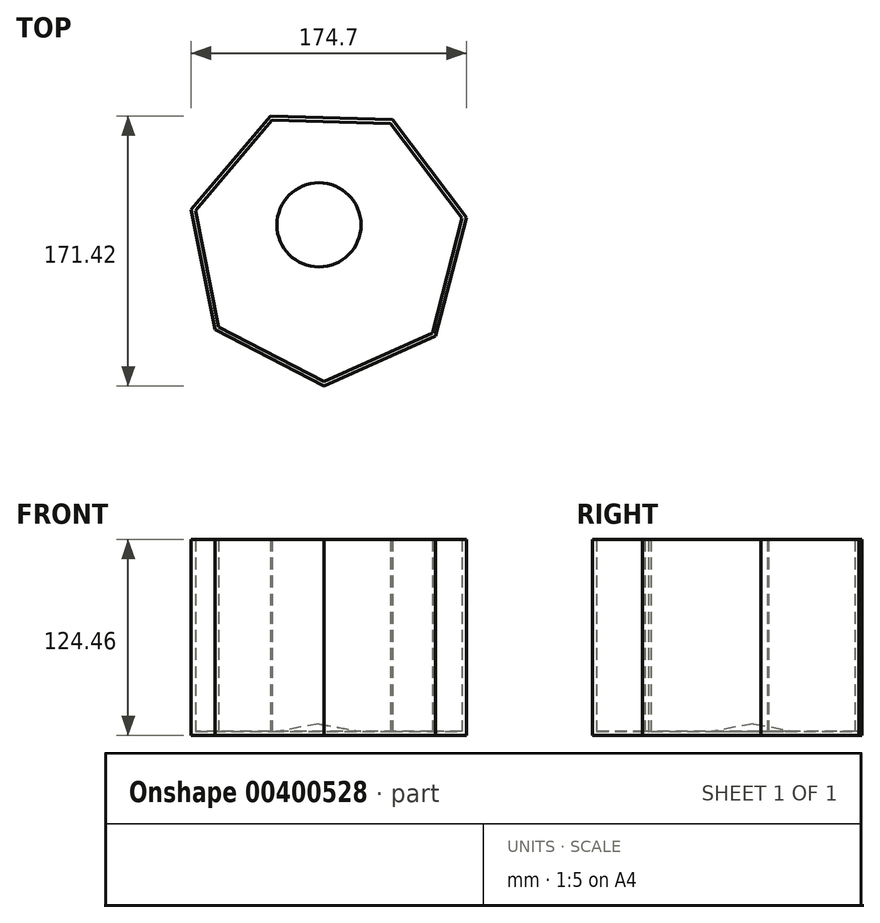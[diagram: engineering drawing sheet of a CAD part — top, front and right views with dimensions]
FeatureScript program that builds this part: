
annotation { "Feature Type Name" : "Feature", "Feature Type Description" : "" }
export const myFeature = defineFeature(function(context is Context, id is Id, definition is map)
    precondition{}
    {
        {
            var Q0;
            Q0=qCreatedBy(makeId("Top.planeOp"),FACE);
            var sketch = newSketch(context, id + "F0", { "sketchPlane" : qUnion([Q0])});
            skCircle(sketch, "E0.cCircle", {"center": v(0, 0) * mm, "radius": 80.76 * mm, "construction": true});
            skLineSegment(sketch, "E0.0", {"start": v(41.16, 79.62) * mm, "end": v(87.91, 17.47) * mm});
            skLineSegment(sketch, "E0.1", {"start": v(87.91, 17.47) * mm, "end": v(68.47, -57.84) * mm});
            skLineSegment(sketch, "E0.2", {"start": v(68.47, -57.84) * mm, "end": v(-2.54, -89.6) * mm});
            skLineSegment(sketch, "E0.3", {"start": v(-2.54, -89.6) * mm, "end": v(-71.63, -53.88) * mm});
            skLineSegment(sketch, "E0.4", {"start": v(-71.63, -53.88) * mm, "end": v(-86.79, 22.4) * mm});
            skLineSegment(sketch, "E0.5", {"start": v(-86.79, 22.4) * mm, "end": v(-36.59, 81.82) * mm});
            skLineSegment(sketch, "E0.6", {"start": v(-36.59, 81.82) * mm, "end": v(41.16, 79.62) * mm});
            skPoint(sketch, "E0.0.midPoint", {"position": v(64.54, 48.54) * mm});
            skSolve(sketch);
        }
        {
            var Q0;
            Q0=makeQuery(id+"F0.imprint","IMPRINT",FACE,{"disambiguationData":[TD([[makeQuery(id+"F0.imprint","IMPRINT",EDGE,{"derivedFrom":sQuery(id+"F0.wireOp",EDGE,"E0.0")}),-1.0]])]});
            extrude(context, id + "F1", {"entities" : qUnion([Q0]), "endBound" : BoundingType.SYMMETRIC, "depth" : 124.46 * mm});
        }
        {
            var Q0;
            Q0=makeQuery(id+"F1.opExtrude","CAP_FACE",FACE,{"disambiguationData":[OSD([sQuery(id+"F0.wireOp",EDGE,"E0.0"),sQuery(id+"F0.wireOp",EDGE,"E0.1"),sQuery(id+"F0.wireOp",EDGE,"E0.2"),sQuery(id+"F0.wireOp",EDGE,"E0.3"),sQuery(id+"F0.wireOp",EDGE,"E0.4"),sQuery(id+"F0.wireOp",EDGE,"E0.5"),sQuery(id+"F0.wireOp",EDGE,"E0.6")])],"isStart":false});
            shell(context, id + "F2", {"entities" : qUnion([Q0]), "thickness" : 2.54 * mm});
        }
        {
            var Q0;
            Q0=makeQuery(id+"F2.opShell","OFFSET_FACE",FACE,{"disambiguationData":[OSD([sQuery(id+"F0.wireOp",EDGE,"E0.0"),sQuery(id+"F0.wireOp",EDGE,"E0.1"),sQuery(id+"F0.wireOp",EDGE,"E0.2"),sQuery(id+"F0.wireOp",EDGE,"E0.3"),sQuery(id+"F0.wireOp",EDGE,"E0.4"),sQuery(id+"F0.wireOp",EDGE,"E0.5"),sQuery(id+"F0.wireOp",EDGE,"E0.6")])]});
            var sketch = newSketch(context, id + "F3", { "sketchPlane" : qUnion([Q0])});
            skCircle(sketch, "E1", {"center": v(-5.67, 12.74) * mm, "radius": 26.73 * mm});
            skLineSegment(sketch, "E2", {"start": v(-21.64, -8.69) * mm, "end": v(-5.67, 12.74) * mm});
            skLineSegment(sketch, "E3", {"start": v(-5.67, 12.74) * mm, "end": v(-19.34, 35.7) * mm});
            skLineSegment(sketch, "E4", {"start": v(-19.34, 35.7) * mm, "end": v(-5.67, 12.74) * mm});
            skLineSegment(sketch, "E5", {"start": v(-5.67, 12.74) * mm, "end": v(21.06, 12.74) * mm});
            skSolve(sketch);
        }
        {
            var Q0;
            Q0 = qSketchRegion(id + "F3", true);
            extrude(context, id + "F4", {"entities" : qUnion([Q0]), "operationType" : NewBodyOperationType.ADD, "depth" : 76.2 * mm, "hasDraft" : true, "draftAngle" : 80 * degree, "draftPullDirection" : true});
        }
    });
